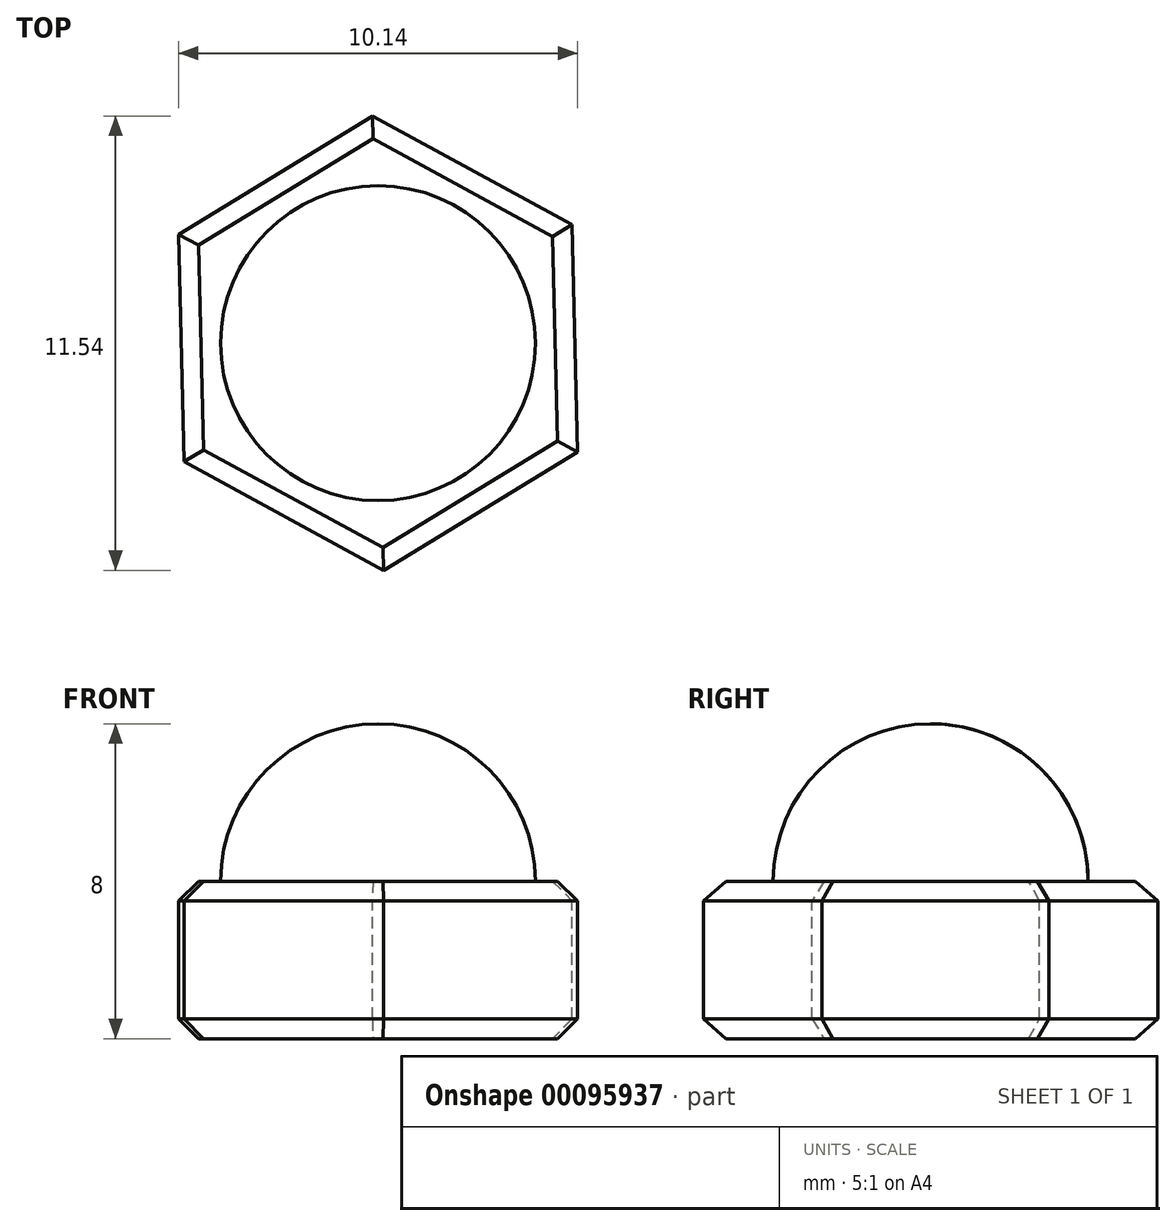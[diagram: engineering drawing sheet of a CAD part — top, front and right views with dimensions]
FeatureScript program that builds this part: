
annotation { "Feature Type Name" : "Feature", "Feature Type Description" : "" }
export const myFeature = defineFeature(function(context is Context, id is Id, definition is map)
    precondition{}
    {
        {
            var Q0;
            Q0=qCreatedBy(makeId("Right.planeOp"),FACE);
            var sketch = newSketch(context, id + "F0", { "sketchPlane" : qUnion([Q0])});
            skArc(sketch, "E0", {"start": v(0, 4) * mm, "mid": v(-2.83, 2.83) * mm, "end": v(-4, 0) * mm});
            skLineSegment(sketch, "E1", {"start": v(0, 0) * mm, "end": v(0, 4) * mm});
            skLineSegment(sketch, "E2", {"start": v(0, 4) * mm, "end": v(0, 0) * mm});
            skLineSegment(sketch, "E3", {"start": v(0, 0) * mm, "end": v(-4, 0) * mm});
            skPoint(sketch, "E4", {"position": v(0, 4) * mm});
            skPoint(sketch, "E5", {"position": v(-4, 0) * mm});
            skSolve(sketch);
        }
        {
            var Q0;
            Q0=makeQuery(id+"F0.imprint","IMPRINT",FACE,{"disambiguationData":[TD([[makeQuery(id+"F0.imprint","IMPRINT",EDGE,{"derivedFrom":sQuery(id+"F0.wireOp",EDGE,"E0")}),1.0]])]});
            var Q1;
            Q1=sQuery(id+"F0.wireOp",EDGE,"E2");
            revolve(context, id + "F1", {"entities" : qUnion([Q0]), "axis" : qUnion([Q1]), "revolveType" : RevolveType.FULL});
        }
        {
            var Q0;
            Q0=makeQuery(id+"F1.opRevolve","SWEPT_FACE",FACE,{"disambiguationData":[OSD([sQuery(id+"F0.wireOp",EDGE,"E3")])]});
            var sketch = newSketch(context, id + "F2", { "sketchPlane" : qUnion([Q0])});
            skCircle(sketch, "E6.cCircle", {"center": v(0, 0) * mm, "radius": 5 * mm, "construction": true});
            skLineSegment(sketch, "E6.0", {"start": v(4.93, -3) * mm, "end": v(-0.14, -5.77) * mm});
            skLineSegment(sketch, "E6.1", {"start": v(-0.14, -5.77) * mm, "end": v(-5.07, -2.76) * mm});
            skLineSegment(sketch, "E6.2", {"start": v(-5.07, -2.76) * mm, "end": v(-4.93, 3) * mm});
            skLineSegment(sketch, "E6.3", {"start": v(-4.93, 3) * mm, "end": v(0.14, 5.77) * mm});
            skLineSegment(sketch, "E6.4", {"start": v(0.14, 5.77) * mm, "end": v(5.07, 2.76) * mm});
            skLineSegment(sketch, "E6.5", {"start": v(5.07, 2.76) * mm, "end": v(4.93, -3) * mm});
            skPoint(sketch, "E6.0.midPoint", {"position": v(2.4, -4.4) * mm});
            skSolve(sketch);
        }
        {
            var Q0;
            Q0 = qSketchRegion(id + "F2", true);
            extrude(context, id + "F3", {"entities" : qUnion([Q0]), "operationType" : NewBodyOperationType.ADD, "depth" : 4 * mm});
        }
        {
            var Q0;
            Q0=makeQuery(id+"F3.opExtrude","CAP_EDGE",EDGE,{"disambiguationData":[OSD([sQuery(id+"F2.wireOp",EDGE,"E6.4")])],"isStart":true});
            var Q1;
            Q1=makeQuery(id+"F3.opExtrude","CAP_EDGE",EDGE,{"disambiguationData":[OSD([sQuery(id+"F2.wireOp",EDGE,"E6.5")])],"isStart":true});
            var Q2;
            Q2=makeQuery(id+"F3.opExtrude","CAP_EDGE",EDGE,{"disambiguationData":[OSD([sQuery(id+"F2.wireOp",EDGE,"E6.0")])],"isStart":true});
            var Q3;
            Q3=makeQuery(id+"F3.opExtrude","CAP_EDGE",EDGE,{"disambiguationData":[OSD([sQuery(id+"F2.wireOp",EDGE,"E6.4")])],"isStart":false});
            var Q4;
            Q4=makeQuery(id+"F3.opExtrude","CAP_EDGE",EDGE,{"disambiguationData":[OSD([sQuery(id+"F2.wireOp",EDGE,"E6.3")])],"isStart":false});
            var Q5;
            Q5=makeQuery(id+"F3.opExtrude","CAP_EDGE",EDGE,{"disambiguationData":[OSD([sQuery(id+"F2.wireOp",EDGE,"E6.3")])],"isStart":true});
            var Q6;
            Q6=makeQuery(id+"F3.opExtrude","CAP_EDGE",EDGE,{"disambiguationData":[OSD([sQuery(id+"F2.wireOp",EDGE,"E6.1")])],"isStart":true});
            var Q7;
            Q7=makeQuery(id+"F3.opExtrude","CAP_EDGE",EDGE,{"disambiguationData":[OSD([sQuery(id+"F2.wireOp",EDGE,"E6.2")])],"isStart":true});
            var Q8;
            Q8=makeQuery(id+"F3.opExtrude","CAP_EDGE",EDGE,{"disambiguationData":[OSD([sQuery(id+"F2.wireOp",EDGE,"E6.0")])],"isStart":false});
            var Q9;
            Q9=makeQuery(id+"F3.opExtrude","CAP_EDGE",EDGE,{"disambiguationData":[OSD([sQuery(id+"F2.wireOp",EDGE,"E6.1")])],"isStart":false});
            var Q10;
            Q10=makeQuery(id+"F3.opExtrude","CAP_EDGE",EDGE,{"disambiguationData":[OSD([sQuery(id+"F2.wireOp",EDGE,"E6.5")])],"isStart":false});
            var Q11;
            Q11=makeQuery(id+"F3.opExtrude","CAP_EDGE",EDGE,{"disambiguationData":[OSD([sQuery(id+"F2.wireOp",EDGE,"E6.2")])],"isStart":false});
            chamfer(context, id + "F4", {"entities" : qUnion([Q0, Q1, Q2, Q3, Q4, Q5, Q6, Q7, Q8, Q9, Q10, Q11]), "width" : .5 * mm, "tangentPropagation" : true});
        }
    });
